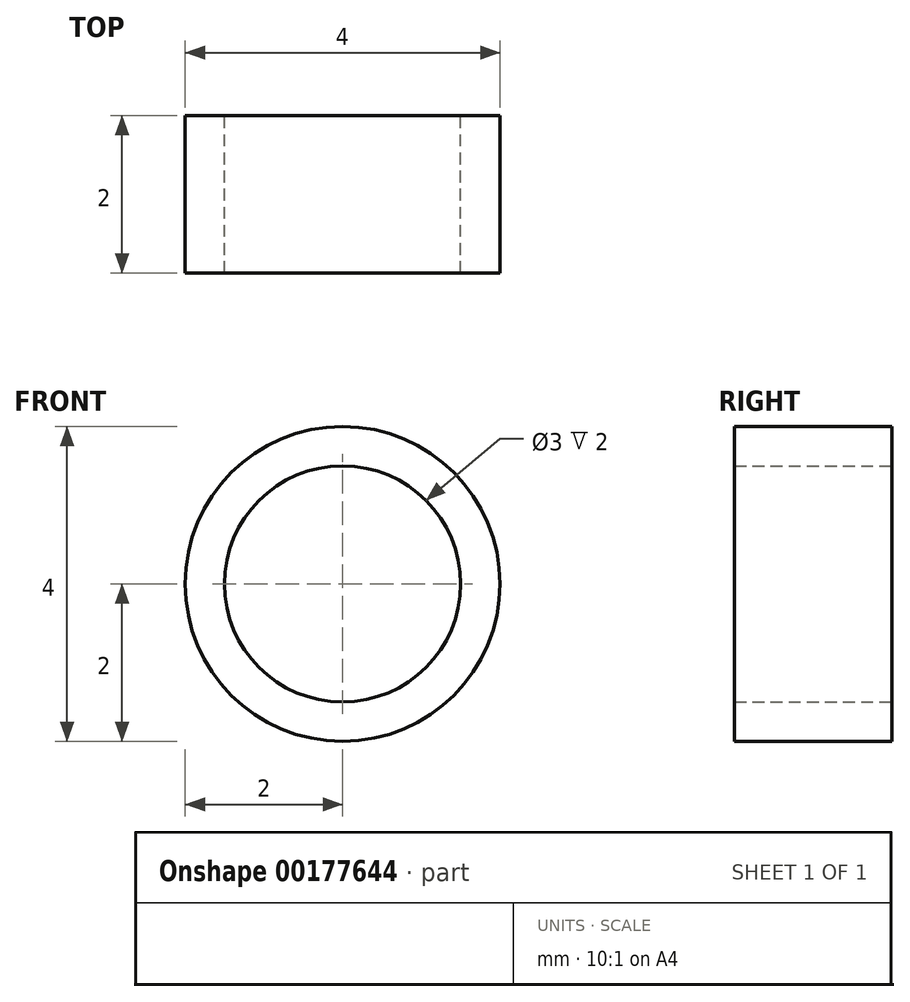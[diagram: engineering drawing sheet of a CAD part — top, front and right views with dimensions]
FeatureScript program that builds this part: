
annotation { "Feature Type Name" : "Feature", "Feature Type Description" : "" }
export const myFeature = defineFeature(function(context is Context, id is Id, definition is map)
    precondition{}
    {
        {
            var Q0;
            Q0=qCreatedBy(makeId("Front.planeOp"),FACE);
            var sketch = newSketch(context, id + "F0", { "sketchPlane" : qUnion([Q0])});
            skCircle(sketch, "E0", {"center": v(0, 0) * mm, "radius": 2 * mm});
            skCircle(sketch, "E1", {"center": v(0, 0) * mm, "radius": 1.5 * mm});
            skSolve(sketch);
        }
        {
            var Q0;
            Q0=qSketchRegion(id+"F0",true);
            extrude(context, id + "F1", {"entities" : qUnion([Q0]), "depth" : 2 * mm});
        }
    });
